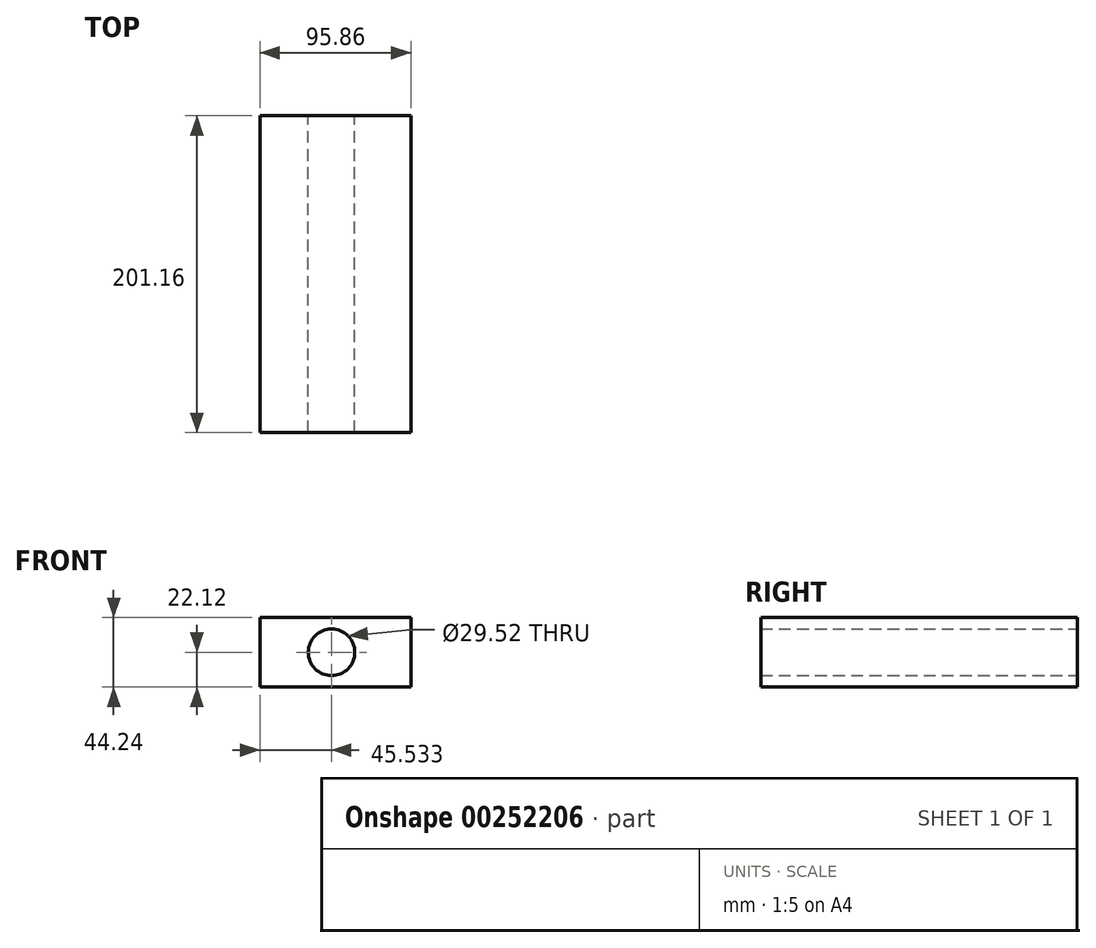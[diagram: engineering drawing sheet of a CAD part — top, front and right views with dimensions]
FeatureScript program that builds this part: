
annotation { "Feature Type Name" : "Feature", "Feature Type Description" : "" }
export const myFeature = defineFeature(function(context is Context, id is Id, definition is map)
    precondition{}
    {
        {
            var Q0;
            Q0=qCreatedBy(makeId("Front.planeOp"),FACE);
            var sketch = newSketch(context, id + "F0", { "sketchPlane" : qUnion([Q0])});
            skLineSegment(sketch, "E0.bottom", {"start": v(-47.93, 22.12) * mm, "end": v(47.93, 22.12) * mm});
            skLineSegment(sketch, "E0.top", {"start": v(-47.93, -22.12) * mm, "end": v(47.93, -22.12) * mm});
            skLineSegment(sketch, "E0.left", {"start": v(-47.93, 22.12) * mm, "end": v(-47.93, -22.12) * mm});
            skLineSegment(sketch, "E0.right", {"start": v(47.93, 22.12) * mm, "end": v(47.93, -22.12) * mm});
            skPoint(sketch, "E0.middle", {"position": v(0, 0) * mm});
            skCircle(sketch, "E1", {"center": v(-2.4, 0) * mm, "radius": 14.76 * mm});
            skSolve(sketch);
        }
        {
            var Q0;
            Q0 = qSketchRegion(id + "F0", true);
            extrude(context, id + "F1", {"entities" : qUnion([Q0]), "endBound" : BoundingType.SYMMETRIC, "depth" : 201.17 * mm});
        }
    });
